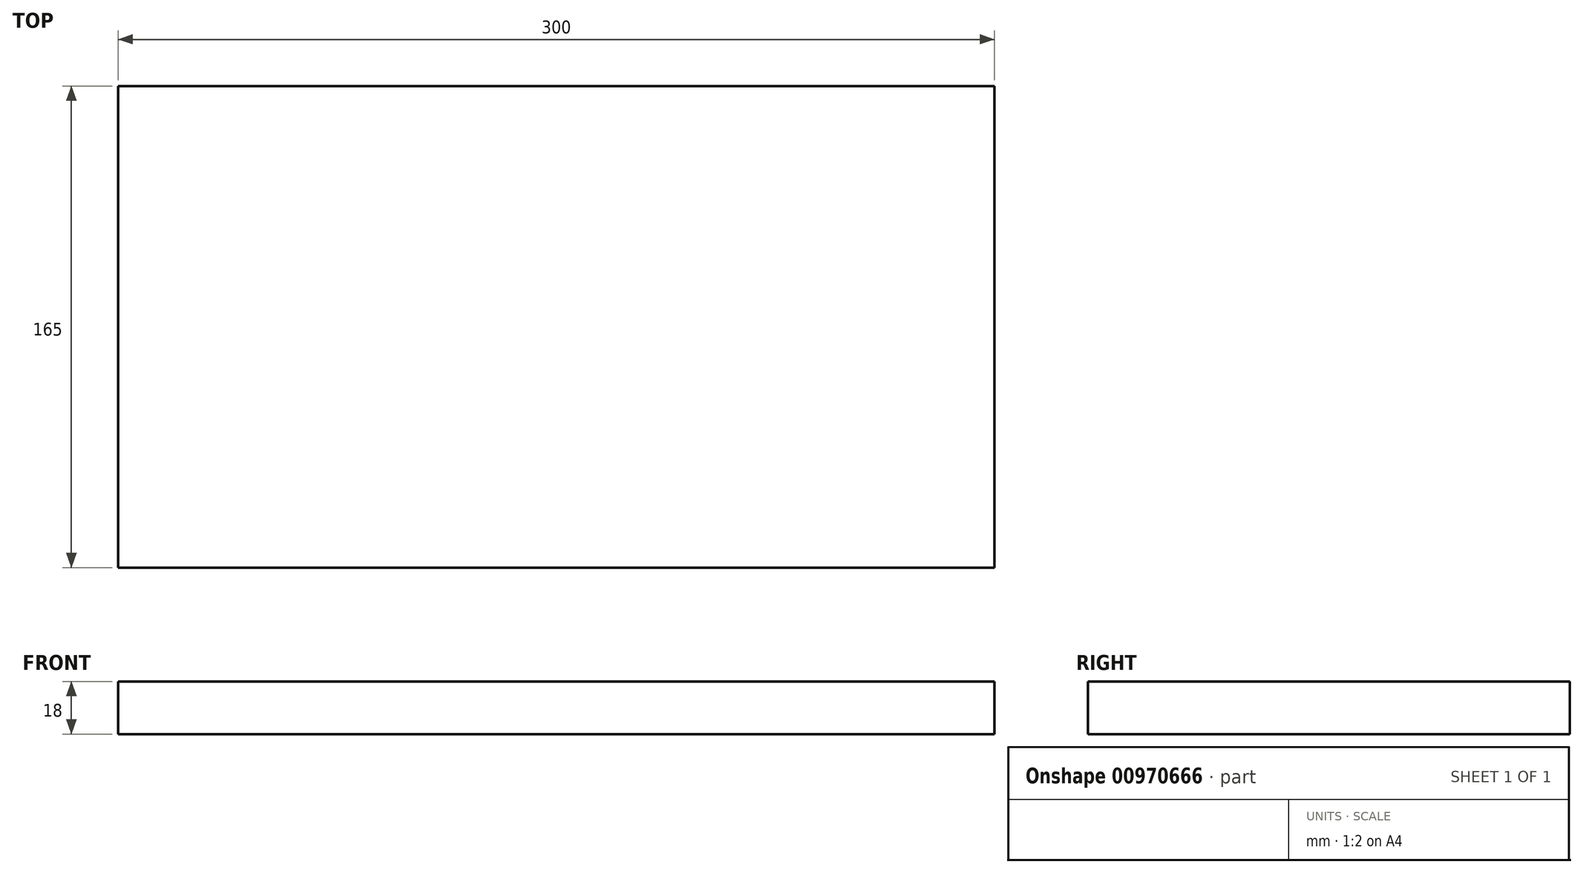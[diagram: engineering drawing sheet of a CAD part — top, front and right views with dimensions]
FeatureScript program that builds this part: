
annotation { "Feature Type Name" : "Feature", "Feature Type Description" : "" }
export const myFeature = defineFeature(function(context is Context, id is Id, definition is map)
    precondition{}
    {
        {
            var Q0;
            Q0=qCreatedBy(makeId("Front.planeOp"),FACE);
            var sketch = newSketch(context, id + "F0", { "sketchPlane" : qUnion([Q0])});
            skLineSegment(sketch, "E0.bottom", {"start": v(-139.36, 10.67) * mm, "end": v(160.64, 10.67) * mm});
            skLineSegment(sketch, "E0.top", {"start": v(-139.36, 28.67) * mm, "end": v(160.64, 28.67) * mm});
            skLineSegment(sketch, "E0.left", {"start": v(-139.36, 10.67) * mm, "end": v(-139.36, 28.67) * mm});
            skLineSegment(sketch, "E0.right", {"start": v(160.64, 10.67) * mm, "end": v(160.64, 28.67) * mm});
            skSolve(sketch);
        }
        {
            var Q0;
            Q0 = qSketchRegion(id + "F0", true);
            extrude(context, id + "F1", {"entities" : qUnion([Q0]), "oppositeDirection" : true, "depth" : 165 * mm, "offsetDistance" : 25 * mm});
        }
    });
